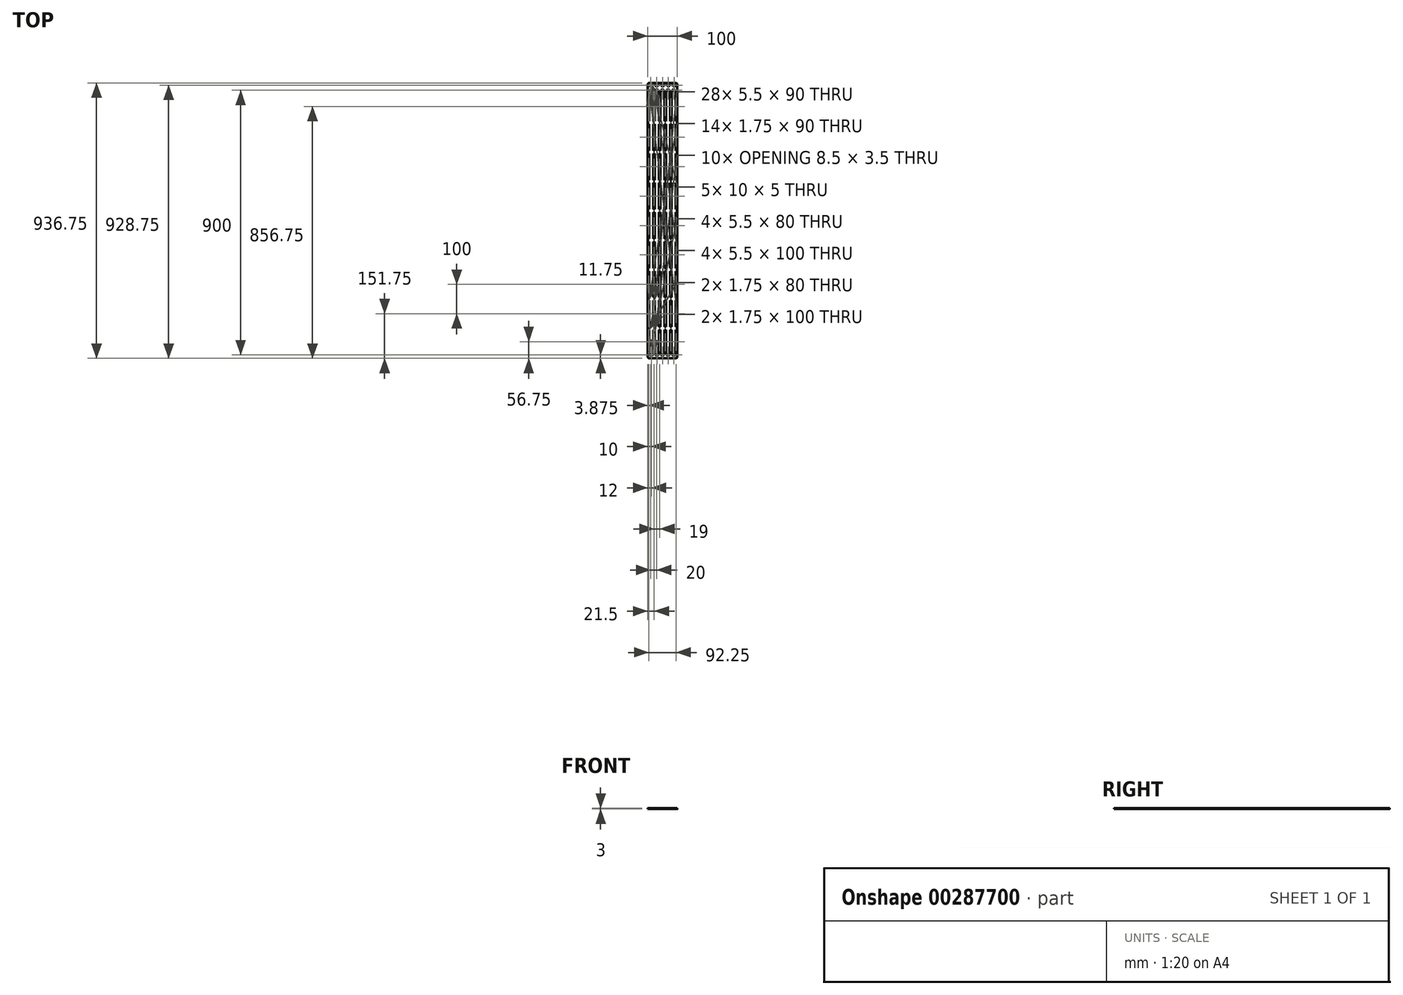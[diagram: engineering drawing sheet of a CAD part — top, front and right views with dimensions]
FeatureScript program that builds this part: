
annotation { "Feature Type Name" : "Feature", "Feature Type Description" : "" }
export const myFeature = defineFeature(function(context is Context, id is Id, definition is map)
    precondition{}
    {
        {
            var Q0;
            Q0=qCreatedBy(makeId("Top.planeOp"),FACE);
            var sketch = newSketch(context, id + "F0", { "sketchPlane" : qUnion([Q0])});
            skLineSegment(sketch, "E0.bottom", {"start": v(-45, 475) * mm, "end": v(45, 475) * mm});
            skLineSegment(sketch, "E0.top", {"start": v(-45, -475) * mm, "end": v(45, -475) * mm});
            skLineSegment(sketch, "E0.left", {"start": v(-50, 470) * mm, "end": v(-50, -456.75) * mm});
            skLineSegment(sketch, "E0.right", {"start": v(50, 470) * mm, "end": v(50, -456.75) * mm});
            skPoint(sketch, "E0.middle", {"position": v(0, 0) * mm});
            skLineSegment(sketch, "E1", {"start": v(-50, 450) * mm, "end": v(50, 450) * mm, "construction": true});
            skLineSegment(sketch, "E2", {"start": v(-50, -450) * mm, "end": v(50, -450) * mm, "construction": true});
            skLineSegment(sketch, "E3.bottom", {"start": v(-3.75, 451.75) * mm, "end": v(3.75, 451.75) * mm});
            skLineSegment(sketch, "E3.top", {"start": v(-3.75, 448.25) * mm, "end": v(3.75, 448.25) * mm});
            skLineSegment(sketch, "E3.left", {"start": v(-4.25, 451.25) * mm, "end": v(-4.25, 448.75) * mm});
            skLineSegment(sketch, "E3.right", {"start": v(4.25, 451.25) * mm, "end": v(4.25, 448.75) * mm});
            skPoint(sketch, "E3.middle", {"position": v(0, 450) * mm});
            skPoint(sketch, "E4.visualSharp", {"position": v(-4.25, 451.75) * mm});
            skArc(sketch, "E4.filletArc", {"start": v(-3.75, 451.75) * mm, "mid": v(-4.1, 451.6) * mm, "end": v(-4.25, 451.25) * mm});
            skPoint(sketch, "E5.visualSharp", {"position": v(-4.25, 448.25) * mm});
            skArc(sketch, "E5.filletArc", {"start": v(-4.25, 448.75) * mm, "mid": v(-4.1, 448.4) * mm, "end": v(-3.75, 448.25) * mm});
            skPoint(sketch, "E6.visualSharp", {"position": v(4.25, 451.75) * mm});
            skArc(sketch, "E6.filletArc", {"start": v(4.25, 451.25) * mm, "mid": v(4.1, 451.6) * mm, "end": v(3.75, 451.75) * mm});
            skPoint(sketch, "E7.visualSharp", {"position": v(4.25, 448.25) * mm});
            skArc(sketch, "E7.filletArc", {"start": v(3.75, 448.25) * mm, "mid": v(4.1, 448.4) * mm, "end": v(4.25, 448.75) * mm});
            skLineSegment(sketch, "E8.1.0.0", {"start": v(15.25, 451.75) * mm, "end": v(22.75, 451.75) * mm});
            skLineSegment(sketch, "E8.1.0.1", {"start": v(23.25, 451.25) * mm, "end": v(23.25, 448.75) * mm});
            skLineSegment(sketch, "E8.1.0.2", {"start": v(14.75, 451.25) * mm, "end": v(14.75, 448.75) * mm});
            skLineSegment(sketch, "E8.1.0.3", {"start": v(15.25, 448.25) * mm, "end": v(22.75, 448.25) * mm});
            skPoint(sketch, "E8.1.0.4", {"position": v(14.75, 448.25) * mm});
            skPoint(sketch, "E8.1.0.5", {"position": v(23.25, 451.75) * mm});
            skPoint(sketch, "E8.1.0.6", {"position": v(19, 450) * mm});
            skPoint(sketch, "E8.1.0.7", {"position": v(23.25, 448.25) * mm});
            skPoint(sketch, "E8.1.0.8", {"position": v(14.75, 451.75) * mm});
            skArc(sketch, "E8.1.0.9", {"start": v(22.75, 448.25) * mm, "mid": v(23.1, 448.4) * mm, "end": v(23.25, 448.75) * mm});
            skArc(sketch, "E8.1.0.10", {"start": v(15.25, 451.75) * mm, "mid": v(14.9, 451.6) * mm, "end": v(14.75, 451.25) * mm});
            skArc(sketch, "E8.1.0.11", {"start": v(14.75, 448.75) * mm, "mid": v(14.9, 448.4) * mm, "end": v(15.25, 448.25) * mm});
            skArc(sketch, "E8.1.0.12", {"start": v(23.25, 451.25) * mm, "mid": v(23.1, 451.6) * mm, "end": v(22.75, 451.75) * mm});
            skLineSegment(sketch, "E8.2.0.0", {"start": v(34.25, 451.75) * mm, "end": v(41.75, 451.75) * mm});
            skLineSegment(sketch, "E8.2.0.1", {"start": v(42.25, 451.25) * mm, "end": v(42.25, 448.75) * mm});
            skLineSegment(sketch, "E8.2.0.2", {"start": v(33.75, 451.25) * mm, "end": v(33.75, 448.75) * mm});
            skLineSegment(sketch, "E8.2.0.3", {"start": v(34.25, 448.25) * mm, "end": v(41.75, 448.25) * mm});
            skPoint(sketch, "E8.2.0.4", {"position": v(33.75, 448.25) * mm});
            skPoint(sketch, "E8.2.0.5", {"position": v(42.25, 451.75) * mm});
            skPoint(sketch, "E8.2.0.6", {"position": v(38, 450) * mm});
            skPoint(sketch, "E8.2.0.7", {"position": v(42.25, 448.25) * mm});
            skPoint(sketch, "E8.2.0.8", {"position": v(33.75, 451.75) * mm});
            skArc(sketch, "E8.2.0.9", {"start": v(41.75, 448.25) * mm, "mid": v(42.1, 448.4) * mm, "end": v(42.25, 448.75) * mm});
            skArc(sketch, "E8.2.0.10", {"start": v(34.25, 451.75) * mm, "mid": v(33.9, 451.6) * mm, "end": v(33.75, 451.25) * mm});
            skArc(sketch, "E8.2.0.11", {"start": v(33.75, 448.75) * mm, "mid": v(33.9, 448.4) * mm, "end": v(34.25, 448.25) * mm});
            skArc(sketch, "E8.2.0.12", {"start": v(42.25, 451.25) * mm, "mid": v(42.1, 451.6) * mm, "end": v(41.75, 451.75) * mm});
            skLineSegment(sketch, "E8.direction1", {"start": v(-4.25, 448.25) * mm, "end": v(14.75, 448.25) * mm, "construction": true});
            skPoint(sketch, "E9.1.0.0", {"position": v(-23.25, 448.25) * mm});
            skPoint(sketch, "E9.1.0.1", {"position": v(-14.75, 448.25) * mm});
            skPoint(sketch, "E9.1.0.2", {"position": v(-19, 450) * mm});
            skPoint(sketch, "E9.1.0.3", {"position": v(-14.75, 451.75) * mm});
            skPoint(sketch, "E9.1.0.4", {"position": v(-23.25, 451.75) * mm});
            skLineSegment(sketch, "E9.1.0.5", {"start": v(-22.75, 451.75) * mm, "end": v(-15.25, 451.75) * mm});
            skLineSegment(sketch, "E9.1.0.6", {"start": v(-22.75, 448.25) * mm, "end": v(-15.25, 448.25) * mm});
            skLineSegment(sketch, "E9.1.0.7", {"start": v(-23.25, 451.25) * mm, "end": v(-23.25, 448.75) * mm});
            skLineSegment(sketch, "E9.1.0.8", {"start": v(-14.75, 451.25) * mm, "end": v(-14.75, 448.75) * mm});
            skArc(sketch, "E9.1.0.9", {"start": v(-14.75, 451.25) * mm, "mid": v(-14.9, 451.6) * mm, "end": v(-15.25, 451.75) * mm});
            skArc(sketch, "E9.1.0.10", {"start": v(-23.25, 448.75) * mm, "mid": v(-23.1, 448.4) * mm, "end": v(-22.75, 448.25) * mm});
            skArc(sketch, "E9.1.0.11", {"start": v(-22.75, 451.75) * mm, "mid": v(-23.1, 451.6) * mm, "end": v(-23.25, 451.25) * mm});
            skArc(sketch, "E9.1.0.12", {"start": v(-15.25, 448.25) * mm, "mid": v(-14.9, 448.4) * mm, "end": v(-14.75, 448.75) * mm});
            skPoint(sketch, "E9.2.0.0", {"position": v(-42.25, 448.25) * mm});
            skPoint(sketch, "E9.2.0.1", {"position": v(-33.75, 448.25) * mm});
            skPoint(sketch, "E9.2.0.2", {"position": v(-38, 450) * mm});
            skPoint(sketch, "E9.2.0.3", {"position": v(-33.75, 451.75) * mm});
            skPoint(sketch, "E9.2.0.4", {"position": v(-42.25, 451.75) * mm});
            skLineSegment(sketch, "E9.2.0.5", {"start": v(-41.75, 451.75) * mm, "end": v(-34.25, 451.75) * mm});
            skLineSegment(sketch, "E9.2.0.6", {"start": v(-41.75, 448.25) * mm, "end": v(-34.25, 448.25) * mm});
            skLineSegment(sketch, "E9.2.0.7", {"start": v(-42.25, 451.25) * mm, "end": v(-42.25, 448.75) * mm});
            skLineSegment(sketch, "E9.2.0.8", {"start": v(-33.75, 451.25) * mm, "end": v(-33.75, 448.75) * mm});
            skArc(sketch, "E9.2.0.9", {"start": v(-33.75, 451.25) * mm, "mid": v(-33.9, 451.6) * mm, "end": v(-34.25, 451.75) * mm});
            skArc(sketch, "E9.2.0.10", {"start": v(-42.25, 448.75) * mm, "mid": v(-42.1, 448.4) * mm, "end": v(-41.75, 448.25) * mm});
            skArc(sketch, "E9.2.0.11", {"start": v(-41.75, 451.75) * mm, "mid": v(-42.1, 451.6) * mm, "end": v(-42.25, 451.25) * mm});
            skArc(sketch, "E9.2.0.12", {"start": v(-34.25, 448.25) * mm, "mid": v(-33.9, 448.4) * mm, "end": v(-33.75, 448.75) * mm});
            skLineSegment(sketch, "E9.direction1", {"start": v(-4.25, 448.25) * mm, "end": v(-23.25, 448.25) * mm, "construction": true});
            skLineSegment(sketch, "E10", {"start": v(-50, 467) * mm, "end": v(50, 467) * mm, "construction": true});
            skLineSegment(sketch, "E11.bottom", {"start": v(-5, 469.5) * mm, "end": v(5, 469.5) * mm});
            skLineSegment(sketch, "E11.top", {"start": v(-5, 464.5) * mm, "end": v(5, 464.5) * mm});
            skLineSegment(sketch, "E11.left", {"start": v(-5, 469.5) * mm, "end": v(-5, 464.5) * mm});
            skLineSegment(sketch, "E11.right", {"start": v(5, 469.5) * mm, "end": v(5, 464.5) * mm});
            skPoint(sketch, "E11.middle", {"position": v(0, 467) * mm});
            skPoint(sketch, "E12.visualSharp", {"position": v(-50, 475) * mm});
            skArc(sketch, "E12.filletArc", {"start": v(-45, 475) * mm, "mid": v(-48.54, 473.54) * mm, "end": v(-50, 470) * mm});
            skPoint(sketch, "E13.visualSharp", {"position": v(50, 475) * mm});
            skArc(sketch, "E13.filletArc", {"start": v(50, 470) * mm, "mid": v(48.54, 473.54) * mm, "end": v(45, 475) * mm});
            skPoint(sketch, "E14.visualSharp", {"position": v(-50, -475) * mm});
            skArc(sketch, "E14.filletArc", {"start": v(-50, -470) * mm, "mid": v(-48.54, -473.54) * mm, "end": v(-45, -475) * mm});
            skPoint(sketch, "E15.visualSharp", {"position": v(50, -475) * mm});
            skArc(sketch, "E15.filletArc", {"start": v(45, -475) * mm, "mid": v(48.54, -473.54) * mm, "end": v(50, -470) * mm});
            skPoint(sketch, "E16.1.0.0", {"position": v(20, 467) * mm});
            skLineSegment(sketch, "E16.1.0.1", {"start": v(25, 469.5) * mm, "end": v(25, 464.5) * mm});
            skLineSegment(sketch, "E16.1.0.2", {"start": v(15, 469.5) * mm, "end": v(25, 469.5) * mm});
            skLineSegment(sketch, "E16.1.0.3", {"start": v(15, 469.5) * mm, "end": v(15, 464.5) * mm});
            skLineSegment(sketch, "E16.1.0.4", {"start": v(15, 464.5) * mm, "end": v(25, 464.5) * mm});
            skPoint(sketch, "E16.2.0.0", {"position": v(40, 467) * mm});
            skLineSegment(sketch, "E16.2.0.1", {"start": v(45, 469.5) * mm, "end": v(45, 464.5) * mm});
            skLineSegment(sketch, "E16.2.0.2", {"start": v(35, 469.5) * mm, "end": v(45, 469.5) * mm});
            skLineSegment(sketch, "E16.2.0.3", {"start": v(35, 469.5) * mm, "end": v(35, 464.5) * mm});
            skLineSegment(sketch, "E16.2.0.4", {"start": v(35, 464.5) * mm, "end": v(45, 464.5) * mm});
            skLineSegment(sketch, "E16.direction1", {"start": v(-5, 464.5) * mm, "end": v(15, 464.5) * mm, "construction": true});
            skLineSegment(sketch, "E17.1.0.0", {"start": v(-15, 469.5) * mm, "end": v(-15, 464.5) * mm});
            skLineSegment(sketch, "E17.1.0.1", {"start": v(-25, 469.5) * mm, "end": v(-25, 464.5) * mm});
            skPoint(sketch, "E17.1.0.2", {"position": v(-20, 467) * mm});
            skLineSegment(sketch, "E17.1.0.3", {"start": v(-25, 464.5) * mm, "end": v(-15, 464.5) * mm});
            skLineSegment(sketch, "E17.1.0.4", {"start": v(-25, 469.5) * mm, "end": v(-15, 469.5) * mm});
            skLineSegment(sketch, "E17.2.0.0", {"start": v(-35, 469.5) * mm, "end": v(-35, 464.5) * mm});
            skLineSegment(sketch, "E17.2.0.1", {"start": v(-45, 469.5) * mm, "end": v(-45, 464.5) * mm});
            skPoint(sketch, "E17.2.0.2", {"position": v(-40, 467) * mm});
            skLineSegment(sketch, "E17.2.0.3", {"start": v(-45, 464.5) * mm, "end": v(-35, 464.5) * mm});
            skLineSegment(sketch, "E17.2.0.4", {"start": v(-45, 469.5) * mm, "end": v(-35, 469.5) * mm});
            skLineSegment(sketch, "E17.direction1", {"start": v(-5, 464.5) * mm, "end": v(-25, 464.5) * mm, "construction": true});
            skArc(sketch, "E18.MirrorCS", {"start": v(-4.25, -448.75) * mm, "mid": v(-4.1, -448.4) * mm, "end": v(-3.75, -448.25) * mm});
            skArc(sketch, "E19.MirrorCS", {"start": v(22.75, -448.25) * mm, "mid": v(23.1, -448.4) * mm, "end": v(23.25, -448.75) * mm});
            skArc(sketch, "E20.MirrorCS", {"start": v(4.25, -451.25) * mm, "mid": v(4.1, -451.6) * mm, "end": v(3.75, -451.75) * mm});
            skArc(sketch, "E21.MirrorCS", {"start": v(-3.75, -451.75) * mm, "mid": v(-4.1, -451.6) * mm, "end": v(-4.25, -451.25) * mm});
            skArc(sketch, "E22.MirrorCS", {"start": v(3.75, -448.25) * mm, "mid": v(4.1, -448.4) * mm, "end": v(4.25, -448.75) * mm});
            skArc(sketch, "E23.MirrorCS", {"start": v(-15.25, -448.25) * mm, "mid": v(-14.9, -448.4) * mm, "end": v(-14.75, -448.75) * mm});
            skArc(sketch, "E24.MirrorCS", {"start": v(-22.75, -451.75) * mm, "mid": v(-23.1, -451.6) * mm, "end": v(-23.25, -451.25) * mm});
            skArc(sketch, "E25.MirrorCS", {"start": v(-34.25, -448.25) * mm, "mid": v(-33.9, -448.4) * mm, "end": v(-33.75, -448.75) * mm});
            skArc(sketch, "E26.MirrorCS", {"start": v(23.25, -451.25) * mm, "mid": v(23.1, -451.6) * mm, "end": v(22.75, -451.75) * mm});
            skArc(sketch, "E27.MirrorCS", {"start": v(33.75, -448.75) * mm, "mid": v(33.9, -448.4) * mm, "end": v(34.25, -448.25) * mm});
            skArc(sketch, "E28.MirrorCS", {"start": v(-42.25, -448.75) * mm, "mid": v(-42.1, -448.4) * mm, "end": v(-41.75, -448.25) * mm});
            skArc(sketch, "E29.MirrorCS", {"start": v(-23.25, -448.75) * mm, "mid": v(-23.1, -448.4) * mm, "end": v(-22.75, -448.25) * mm});
            skArc(sketch, "E30.MirrorCS", {"start": v(42.25, -451.25) * mm, "mid": v(42.1, -451.6) * mm, "end": v(41.75, -451.75) * mm});
            skArc(sketch, "E31.MirrorCS", {"start": v(-41.75, -451.75) * mm, "mid": v(-42.1, -451.6) * mm, "end": v(-42.25, -451.25) * mm});
            skArc(sketch, "E32.MirrorCS", {"start": v(14.75, -448.75) * mm, "mid": v(14.9, -448.4) * mm, "end": v(15.25, -448.25) * mm});
            skArc(sketch, "E33.MirrorCS", {"start": v(34.25, -451.75) * mm, "mid": v(33.9, -451.6) * mm, "end": v(33.75, -451.25) * mm});
            skArc(sketch, "E34.MirrorCS", {"start": v(-33.75, -451.25) * mm, "mid": v(-33.9, -451.6) * mm, "end": v(-34.25, -451.75) * mm});
            skArc(sketch, "E35.MirrorCS", {"start": v(-14.75, -451.25) * mm, "mid": v(-14.9, -451.6) * mm, "end": v(-15.25, -451.75) * mm});
            skArc(sketch, "E36.MirrorCS", {"start": v(15.25, -451.75) * mm, "mid": v(14.9, -451.6) * mm, "end": v(14.75, -451.25) * mm});
            skArc(sketch, "E37.MirrorCS", {"start": v(41.75, -448.25) * mm, "mid": v(42.1, -448.4) * mm, "end": v(42.25, -448.75) * mm});
            skLineSegment(sketch, "E38.MirrorCS", {"start": v(-14.75, -451.25) * mm, "end": v(-14.75, -448.75) * mm});
            skLineSegment(sketch, "E39.MirrorCS", {"start": v(-22.75, -448.25) * mm, "end": v(-15.25, -448.25) * mm});
            skLineSegment(sketch, "E40.MirrorCS", {"start": v(-3.75, -448.25) * mm, "end": v(3.75, -448.25) * mm});
            skPoint(sketch, "E41.MirrorP", {"position": v(33.75, -448.25) * mm});
            skLineSegment(sketch, "E42.MirrorCS", {"start": v(34.25, -448.25) * mm, "end": v(41.75, -448.25) * mm});
            skLineSegment(sketch, "E43.MirrorCS", {"start": v(-42.25, -451.25) * mm, "end": v(-42.25, -448.75) * mm});
            skPoint(sketch, "E44.MirrorP", {"position": v(19, -450) * mm});
            skPoint(sketch, "E45.MirrorP", {"position": v(-23.25, -448.25) * mm});
            skPoint(sketch, "E46.MirrorP", {"position": v(-4.25, -451.75) * mm});
            skLineSegment(sketch, "E47.MirrorCS", {"start": v(-23.25, -451.25) * mm, "end": v(-23.25, -448.75) * mm});
            skLineSegment(sketch, "E48.MirrorCS", {"start": v(15.25, -448.25) * mm, "end": v(22.75, -448.25) * mm});
            skPoint(sketch, "E49.MirrorP", {"position": v(23.25, -451.75) * mm});
            skLineSegment(sketch, "E50.MirrorCS", {"start": v(33.75, -451.25) * mm, "end": v(33.75, -448.75) * mm});
            skLineSegment(sketch, "E51.MirrorCS", {"start": v(-41.75, -448.25) * mm, "end": v(-34.25, -448.25) * mm});
            skLineSegment(sketch, "E52.MirrorCS", {"start": v(14.75, -451.25) * mm, "end": v(14.75, -448.75) * mm});
            skPoint(sketch, "E53.MirrorP", {"position": v(14.75, -448.25) * mm});
            skLineSegment(sketch, "E54.MirrorCS", {"start": v(42.25, -451.25) * mm, "end": v(42.25, -448.75) * mm});
            skLineSegment(sketch, "E55.MirrorCS", {"start": v(-41.75, -451.75) * mm, "end": v(-34.25, -451.75) * mm});
            skPoint(sketch, "E56.MirrorP", {"position": v(0, -450) * mm});
            skLineSegment(sketch, "E57.MirrorCS", {"start": v(4.25, -451.25) * mm, "end": v(4.25, -448.75) * mm});
            skLineSegment(sketch, "E58.MirrorCS", {"start": v(-4.25, -451.25) * mm, "end": v(-4.25, -448.75) * mm});
            skLineSegment(sketch, "E59.MirrorCS", {"start": v(-3.75, -451.75) * mm, "end": v(3.75, -451.75) * mm});
            skLineSegment(sketch, "E60.MirrorCS", {"start": v(23.25, -451.25) * mm, "end": v(23.25, -448.75) * mm});
            skLineSegment(sketch, "E61.MirrorCS", {"start": v(15.25, -451.75) * mm, "end": v(22.75, -451.75) * mm});
            skLineSegment(sketch, "E62.MirrorCS", {"start": v(-22.75, -451.75) * mm, "end": v(-15.25, -451.75) * mm});
            skLineSegment(sketch, "E63.MirrorCS", {"start": v(-4.25, -448.25) * mm, "end": v(-23.25, -448.25) * mm, "construction": true});
            skLineSegment(sketch, "E64.MirrorCS", {"start": v(34.25, -451.75) * mm, "end": v(41.75, -451.75) * mm});
            skPoint(sketch, "E65.MirrorP", {"position": v(-23.25, -451.75) * mm});
            skPoint(sketch, "E66.MirrorP", {"position": v(-42.25, -451.75) * mm});
            skPoint(sketch, "E67.MirrorP", {"position": v(-33.75, -448.25) * mm});
            skPoint(sketch, "E68.MirrorP", {"position": v(4.25, -451.75) * mm});
            skPoint(sketch, "E69.MirrorP", {"position": v(42.25, -448.25) * mm});
            skLineSegment(sketch, "E70.MirrorCS", {"start": v(-4.25, -448.25) * mm, "end": v(14.75, -448.25) * mm, "construction": true});
            skPoint(sketch, "E71.MirrorP", {"position": v(4.25, -448.25) * mm});
            skPoint(sketch, "E72.MirrorP", {"position": v(-14.75, -451.75) * mm});
            skPoint(sketch, "E73.MirrorP", {"position": v(-33.75, -451.75) * mm});
            skPoint(sketch, "E74.MirrorP", {"position": v(-42.25, -448.25) * mm});
            skPoint(sketch, "E75.MirrorP", {"position": v(38, -450) * mm});
            skPoint(sketch, "E76.MirrorP", {"position": v(14.75, -451.75) * mm});
            skPoint(sketch, "E77.MirrorP", {"position": v(33.75, -451.75) * mm});
            skPoint(sketch, "E78.MirrorP", {"position": v(-19, -450) * mm});
            skPoint(sketch, "E79.MirrorP", {"position": v(-38, -450) * mm});
            skPoint(sketch, "E80.MirrorP", {"position": v(-4.25, -448.25) * mm});
            skPoint(sketch, "E81.MirrorP", {"position": v(42.25, -451.75) * mm});
            skLineSegment(sketch, "E82.MirrorCS", {"start": v(-33.75, -451.25) * mm, "end": v(-33.75, -448.75) * mm});
            skPoint(sketch, "E83.MirrorP", {"position": v(23.25, -448.25) * mm});
            skPoint(sketch, "E84.MirrorP", {"position": v(-14.75, -448.25) * mm});
            skLineSegment(sketch, "E85", {"start": v(-45, -461.75) * mm, "end": v(45, -461.75) * mm});
            skArc(sketch, "E86.filletArc", {"start": v(-50, -456.75) * mm, "mid": v(-48.54, -460.29) * mm, "end": v(-45, -461.75) * mm});
            skArc(sketch, "E87.filletArc", {"start": v(45, -461.75) * mm, "mid": v(48.54, -460.29) * mm, "end": v(50, -456.75) * mm});
            skLineSegment(sketch, "E88.bottom", {"start": v(-31.25, 445) * mm, "end": v(-25.75, 445) * mm});
            skLineSegment(sketch, "E88.top", {"start": v(-31.25, -445) * mm, "end": v(-25.75, -445) * mm});
            skLineSegment(sketch, "E88.left", {"start": v(-31.25, 445) * mm, "end": v(-31.25, -445) * mm});
            skLineSegment(sketch, "E88.right", {"start": v(-25.75, 445) * mm, "end": v(-25.75, -445) * mm});
            skLineSegment(sketch, "E89.1.0.0", {"start": v(-12.25, 445) * mm, "end": v(-12.25, -445) * mm});
            skLineSegment(sketch, "E89.1.0.1", {"start": v(-12.25, 445) * mm, "end": v(-6.75, 445) * mm});
            skLineSegment(sketch, "E89.1.0.2", {"start": v(-6.75, 445) * mm, "end": v(-6.75, -445) * mm});
            skLineSegment(sketch, "E89.1.0.3", {"start": v(-12.25, -445) * mm, "end": v(-6.75, -445) * mm});
            skLineSegment(sketch, "E89.2.0.0", {"start": v(6.75, 445) * mm, "end": v(6.75, -445) * mm});
            skLineSegment(sketch, "E89.2.0.1", {"start": v(6.75, 445) * mm, "end": v(12.25, 445) * mm});
            skLineSegment(sketch, "E89.2.0.2", {"start": v(12.25, 445) * mm, "end": v(12.25, -445) * mm});
            skLineSegment(sketch, "E89.2.0.3", {"start": v(6.75, -445) * mm, "end": v(12.25, -445) * mm});
            skLineSegment(sketch, "E89.3.0.0", {"start": v(25.75, 445) * mm, "end": v(25.75, -445) * mm});
            skLineSegment(sketch, "E89.3.0.1", {"start": v(25.75, 445) * mm, "end": v(31.25, 445) * mm});
            skLineSegment(sketch, "E89.3.0.2", {"start": v(31.25, 445) * mm, "end": v(31.25, -445) * mm});
            skLineSegment(sketch, "E89.3.0.3", {"start": v(25.75, -445) * mm, "end": v(31.25, -445) * mm});
            skLineSegment(sketch, "E89.direction1", {"start": v(-31.25, -445) * mm, "end": v(-12.25, -445) * mm, "construction": true});
            skLineSegment(sketch, "E90", {"start": v(-47, 445) * mm, "end": v(-45.25, 445) * mm});
            skLineSegment(sketch, "E91", {"start": v(-45.25, 445) * mm, "end": v(-45.25, -445) * mm});
            skLineSegment(sketch, "E92", {"start": v(-45.25, -445) * mm, "end": v(-47, -445) * mm});
            skLineSegment(sketch, "E93", {"start": v(-47, -445) * mm, "end": v(-47, 445) * mm});
            skLineSegment(sketch, "E94.MirrorCS", {"start": v(47, 445) * mm, "end": v(45.25, 445) * mm});
            skLineSegment(sketch, "E95.MirrorCS", {"start": v(47, -445) * mm, "end": v(47, 445) * mm});
            skLineSegment(sketch, "E96.MirrorCS", {"start": v(45.25, 445) * mm, "end": v(45.25, -445) * mm});
            skLineSegment(sketch, "E97.MirrorCS", {"start": v(45.25, -445) * mm, "end": v(47, -445) * mm});
            skLineSegment(sketch, "E98", {"start": v(-47, 345) * mm, "end": v(-45.25, 345) * mm});
            skLineSegment(sketch, "E99", {"start": v(-31.25, 345) * mm, "end": v(-25.75, 345) * mm});
            skLineSegment(sketch, "E100", {"start": v(-12.25, 345) * mm, "end": v(-6.75, 345) * mm});
            skLineSegment(sketch, "E101", {"start": v(6.75, 345) * mm, "end": v(12.25, 345) * mm});
            skLineSegment(sketch, "E102", {"start": v(25.75, 345) * mm, "end": v(31.25, 345) * mm});
            skLineSegment(sketch, "E103", {"start": v(45.25, 345) * mm, "end": v(47, 345) * mm});
            skLineSegment(sketch, "E104", {"start": v(-47, 335) * mm, "end": v(-45.25, 335) * mm});
            skLineSegment(sketch, "E105", {"start": v(-31.25, 335) * mm, "end": v(-25.75, 335) * mm});
            skLineSegment(sketch, "E106", {"start": v(-12.25, 335) * mm, "end": v(-6.75, 335) * mm});
            skLineSegment(sketch, "E107", {"start": v(6.75, 335) * mm, "end": v(12.25, 335) * mm});
            skLineSegment(sketch, "E108", {"start": v(25.75, 335) * mm, "end": v(31.25, 335) * mm});
            skLineSegment(sketch, "E109", {"start": v(45.25, 335) * mm, "end": v(47, 335) * mm});
            skLineSegment(sketch, "E110.0.1.0", {"start": v(-47, 245) * mm, "end": v(-45.25, 245) * mm});
            skLineSegment(sketch, "E110.0.1.1", {"start": v(-47, 235) * mm, "end": v(-45.25, 235) * mm});
            skLineSegment(sketch, "E110.0.1.2", {"start": v(-31.25, 245) * mm, "end": v(-25.75, 245) * mm});
            skLineSegment(sketch, "E110.0.1.3", {"start": v(-31.25, 235) * mm, "end": v(-25.75, 235) * mm});
            skLineSegment(sketch, "E110.0.1.4", {"start": v(-12.25, 245) * mm, "end": v(-6.75, 245) * mm});
            skLineSegment(sketch, "E110.0.1.5", {"start": v(-12.25, 235) * mm, "end": v(-6.75, 235) * mm});
            skLineSegment(sketch, "E110.0.1.6", {"start": v(6.75, 245) * mm, "end": v(12.25, 245) * mm});
            skLineSegment(sketch, "E110.0.1.7", {"start": v(6.75, 235) * mm, "end": v(12.25, 235) * mm});
            skLineSegment(sketch, "E110.0.1.8", {"start": v(25.75, 245) * mm, "end": v(31.25, 245) * mm});
            skLineSegment(sketch, "E110.0.1.9", {"start": v(25.75, 235) * mm, "end": v(31.25, 235) * mm});
            skLineSegment(sketch, "E110.0.1.10", {"start": v(45.25, 245) * mm, "end": v(47, 245) * mm});
            skLineSegment(sketch, "E110.0.1.11", {"start": v(45.25, 235) * mm, "end": v(47, 235) * mm});
            skLineSegment(sketch, "E110.0.2.0", {"start": v(-47, 145) * mm, "end": v(-45.25, 145) * mm});
            skLineSegment(sketch, "E110.0.2.1", {"start": v(-47, 135) * mm, "end": v(-45.25, 135) * mm});
            skLineSegment(sketch, "E110.0.2.2", {"start": v(-31.25, 145) * mm, "end": v(-25.75, 145) * mm});
            skLineSegment(sketch, "E110.0.2.3", {"start": v(-31.25, 135) * mm, "end": v(-25.75, 135) * mm});
            skLineSegment(sketch, "E110.0.2.4", {"start": v(-12.25, 145) * mm, "end": v(-6.75, 145) * mm});
            skLineSegment(sketch, "E110.0.2.5", {"start": v(-12.25, 135) * mm, "end": v(-6.75, 135) * mm});
            skLineSegment(sketch, "E110.0.2.6", {"start": v(6.75, 145) * mm, "end": v(12.25, 145) * mm});
            skLineSegment(sketch, "E110.0.2.7", {"start": v(6.75, 135) * mm, "end": v(12.25, 135) * mm});
            skLineSegment(sketch, "E110.0.2.8", {"start": v(25.75, 145) * mm, "end": v(31.25, 145) * mm});
            skLineSegment(sketch, "E110.0.2.9", {"start": v(25.75, 135) * mm, "end": v(31.25, 135) * mm});
            skLineSegment(sketch, "E110.0.2.10", {"start": v(45.25, 145) * mm, "end": v(47, 145) * mm});
            skLineSegment(sketch, "E110.0.2.11", {"start": v(45.25, 135) * mm, "end": v(47, 135) * mm});
            skLineSegment(sketch, "E110.0.3.0", {"start": v(-47, 45) * mm, "end": v(-45.25, 45) * mm});
            skLineSegment(sketch, "E110.0.3.1", {"start": v(-47, 35) * mm, "end": v(-45.25, 35) * mm});
            skLineSegment(sketch, "E110.0.3.2", {"start": v(-31.25, 45) * mm, "end": v(-25.75, 45) * mm});
            skLineSegment(sketch, "E110.0.3.3", {"start": v(-31.25, 35) * mm, "end": v(-25.75, 35) * mm});
            skLineSegment(sketch, "E110.0.3.4", {"start": v(-12.25, 45) * mm, "end": v(-6.75, 45) * mm});
            skLineSegment(sketch, "E110.0.3.5", {"start": v(-12.25, 35) * mm, "end": v(-6.75, 35) * mm});
            skLineSegment(sketch, "E110.0.3.6", {"start": v(6.75, 45) * mm, "end": v(12.25, 45) * mm});
            skLineSegment(sketch, "E110.0.3.7", {"start": v(6.75, 35) * mm, "end": v(12.25, 35) * mm});
            skLineSegment(sketch, "E110.0.3.8", {"start": v(25.75, 45) * mm, "end": v(31.25, 45) * mm});
            skLineSegment(sketch, "E110.0.3.9", {"start": v(25.75, 35) * mm, "end": v(31.25, 35) * mm});
            skLineSegment(sketch, "E110.0.3.10", {"start": v(45.25, 45) * mm, "end": v(47, 45) * mm});
            skLineSegment(sketch, "E110.0.3.11", {"start": v(45.25, 35) * mm, "end": v(47, 35) * mm});
            skLineSegment(sketch, "E110.0.4.0", {"start": v(-47, -55) * mm, "end": v(-45.25, -55) * mm});
            skLineSegment(sketch, "E110.0.4.1", {"start": v(-47, -65) * mm, "end": v(-45.25, -65) * mm});
            skLineSegment(sketch, "E110.0.4.2", {"start": v(-31.25, -55) * mm, "end": v(-25.75, -55) * mm});
            skLineSegment(sketch, "E110.0.4.3", {"start": v(-31.25, -65) * mm, "end": v(-25.75, -65) * mm});
            skLineSegment(sketch, "E110.0.4.4", {"start": v(-12.25, -55) * mm, "end": v(-6.75, -55) * mm});
            skLineSegment(sketch, "E110.0.4.5", {"start": v(-12.25, -65) * mm, "end": v(-6.75, -65) * mm});
            skLineSegment(sketch, "E110.0.4.6", {"start": v(6.75, -55) * mm, "end": v(12.25, -55) * mm});
            skLineSegment(sketch, "E110.0.4.7", {"start": v(6.75, -65) * mm, "end": v(12.25, -65) * mm});
            skLineSegment(sketch, "E110.0.4.8", {"start": v(25.75, -55) * mm, "end": v(31.25, -55) * mm});
            skLineSegment(sketch, "E110.0.4.9", {"start": v(25.75, -65) * mm, "end": v(31.25, -65) * mm});
            skLineSegment(sketch, "E110.0.4.10", {"start": v(45.25, -55) * mm, "end": v(47, -55) * mm});
            skLineSegment(sketch, "E110.0.4.11", {"start": v(45.25, -65) * mm, "end": v(47, -65) * mm});
            skLineSegment(sketch, "E110.0.5.0", {"start": v(-47, -155) * mm, "end": v(-45.25, -155) * mm});
            skLineSegment(sketch, "E110.0.5.1", {"start": v(-47, -165) * mm, "end": v(-45.25, -165) * mm});
            skLineSegment(sketch, "E110.0.5.2", {"start": v(-31.25, -155) * mm, "end": v(-25.75, -155) * mm});
            skLineSegment(sketch, "E110.0.5.3", {"start": v(-31.25, -165) * mm, "end": v(-25.75, -165) * mm});
            skLineSegment(sketch, "E110.0.5.4", {"start": v(-12.25, -155) * mm, "end": v(-6.75, -155) * mm});
            skLineSegment(sketch, "E110.0.5.5", {"start": v(-12.25, -165) * mm, "end": v(-6.75, -165) * mm});
            skLineSegment(sketch, "E110.0.5.6", {"start": v(6.75, -155) * mm, "end": v(12.25, -155) * mm});
            skLineSegment(sketch, "E110.0.5.7", {"start": v(6.75, -165) * mm, "end": v(12.25, -165) * mm});
            skLineSegment(sketch, "E110.0.5.8", {"start": v(25.75, -155) * mm, "end": v(31.25, -155) * mm});
            skLineSegment(sketch, "E110.0.5.9", {"start": v(25.75, -165) * mm, "end": v(31.25, -165) * mm});
            skLineSegment(sketch, "E110.0.5.10", {"start": v(45.25, -155) * mm, "end": v(47, -155) * mm});
            skLineSegment(sketch, "E110.0.5.11", {"start": v(45.25, -165) * mm, "end": v(47, -165) * mm});
            skLineSegment(sketch, "E110.0.6.0", {"start": v(-47, -255) * mm, "end": v(-45.25, -255) * mm});
            skLineSegment(sketch, "E110.0.6.1", {"start": v(-47, -265) * mm, "end": v(-45.25, -265) * mm});
            skLineSegment(sketch, "E110.0.6.2", {"start": v(-31.25, -255) * mm, "end": v(-25.75, -255) * mm});
            skLineSegment(sketch, "E110.0.6.3", {"start": v(-31.25, -265) * mm, "end": v(-25.75, -265) * mm});
            skLineSegment(sketch, "E110.0.6.4", {"start": v(-12.25, -255) * mm, "end": v(-6.75, -255) * mm});
            skLineSegment(sketch, "E110.0.6.5", {"start": v(-12.25, -265) * mm, "end": v(-6.75, -265) * mm});
            skLineSegment(sketch, "E110.0.6.6", {"start": v(6.75, -255) * mm, "end": v(12.25, -255) * mm});
            skLineSegment(sketch, "E110.0.6.7", {"start": v(6.75, -265) * mm, "end": v(12.25, -265) * mm});
            skLineSegment(sketch, "E110.0.6.8", {"start": v(25.75, -255) * mm, "end": v(31.25, -255) * mm});
            skLineSegment(sketch, "E110.0.6.9", {"start": v(25.75, -265) * mm, "end": v(31.25, -265) * mm});
            skLineSegment(sketch, "E110.0.6.10", {"start": v(45.25, -255) * mm, "end": v(47, -255) * mm});
            skLineSegment(sketch, "E110.0.6.11", {"start": v(45.25, -265) * mm, "end": v(47, -265) * mm});
            skLineSegment(sketch, "E110.0.7.0", {"start": v(-47, -355) * mm, "end": v(-45.25, -355) * mm});
            skLineSegment(sketch, "E110.0.7.1", {"start": v(-47, -365) * mm, "end": v(-45.25, -365) * mm});
            skLineSegment(sketch, "E110.0.7.2", {"start": v(-31.25, -355) * mm, "end": v(-25.75, -355) * mm});
            skLineSegment(sketch, "E110.0.7.3", {"start": v(-31.25, -365) * mm, "end": v(-25.75, -365) * mm});
            skLineSegment(sketch, "E110.0.7.4", {"start": v(-12.25, -355) * mm, "end": v(-6.75, -355) * mm});
            skLineSegment(sketch, "E110.0.7.5", {"start": v(-12.25, -365) * mm, "end": v(-6.75, -365) * mm});
            skLineSegment(sketch, "E110.0.7.6", {"start": v(6.75, -355) * mm, "end": v(12.25, -355) * mm});
            skLineSegment(sketch, "E110.0.7.7", {"start": v(6.75, -365) * mm, "end": v(12.25, -365) * mm});
            skLineSegment(sketch, "E110.0.7.8", {"start": v(25.75, -355) * mm, "end": v(31.25, -355) * mm});
            skLineSegment(sketch, "E110.0.7.9", {"start": v(25.75, -365) * mm, "end": v(31.25, -365) * mm});
            skLineSegment(sketch, "E110.0.7.10", {"start": v(45.25, -355) * mm, "end": v(47, -355) * mm});
            skLineSegment(sketch, "E110.0.7.11", {"start": v(45.25, -365) * mm, "end": v(47, -365) * mm});
            skLineSegment(sketch, "E110.direction1", {"start": v(-47, 335) * mm, "end": v(-22, 335) * mm, "construction": true});
            skLineSegment(sketch, "E110.direction2", {"start": v(-47, 335) * mm, "end": v(-47, 235) * mm, "construction": true});
            skSolve(sketch);
        }
        {
            var Q0;
            {var subQ0=sQuery(id+"F0.wireOp",EDGE,"E110.0.5.0");Q0=makeQuery(id+"F0.imprint","IMPRINT",FACE,{"disambiguationData":[TD([[makeQuery(id+"F0.imprint","IMPRINT",EDGE,{"derivedFrom":subQ0}),-1.0]])]});}
            var Q1;
            {var subQ0=sQuery(id+"F0.wireOp",EDGE,"E110.0.5.2");Q1=makeQuery(id+"F0.imprint","IMPRINT",FACE,{"disambiguationData":[TD([[makeQuery(id+"F0.imprint","IMPRINT",EDGE,{"derivedFrom":subQ0}),-1.0]])]});}
            var Q2;
            {var subQ0=sQuery(id+"F0.wireOp",EDGE,"E110.0.5.4");Q2=makeQuery(id+"F0.imprint","IMPRINT",FACE,{"disambiguationData":[TD([[makeQuery(id+"F0.imprint","IMPRINT",EDGE,{"derivedFrom":subQ0}),-1.0]])]});}
            var Q3;
            {var subQ0=sQuery(id+"F0.wireOp",EDGE,"E110.0.5.6");Q3=makeQuery(id+"F0.imprint","IMPRINT",FACE,{"disambiguationData":[TD([[makeQuery(id+"F0.imprint","IMPRINT",EDGE,{"derivedFrom":subQ0}),-1.0]])]});}
            var Q4;
            {var subQ0=sQuery(id+"F0.wireOp",EDGE,"E110.0.5.8");Q4=makeQuery(id+"F0.imprint","IMPRINT",FACE,{"disambiguationData":[TD([[makeQuery(id+"F0.imprint","IMPRINT",EDGE,{"derivedFrom":subQ0}),-1.0]])]});}
            var Q5;
            {var subQ0=sQuery(id+"F0.wireOp",EDGE,"E110.0.5.10");Q5=makeQuery(id+"F0.imprint","IMPRINT",FACE,{"disambiguationData":[TD([[makeQuery(id+"F0.imprint","IMPRINT",EDGE,{"derivedFrom":subQ0}),-1.0]])]});}
            var Q6;
            Q6=makeQuery(id+"F0.imprint","IMPRINT",FACE,{"disambiguationData":[TD([[makeQuery(id+"F0.imprint","IMPRINT",EDGE,{"derivedFrom":sQuery(id+"F0.wireOp",EDGE,"E0.bottom")}),-1.0]])]});
            var Q7;
            {var subQ0=sQuery(id+"F0.wireOp",EDGE,"E110.0.6.0");Q7=makeQuery(id+"F0.imprint","IMPRINT",FACE,{"disambiguationData":[TD([[makeQuery(id+"F0.imprint","IMPRINT",EDGE,{"derivedFrom":subQ0}),-1.0]])]});}
            var Q8;
            {var subQ0=sQuery(id+"F0.wireOp",EDGE,"E110.0.6.2");Q8=makeQuery(id+"F0.imprint","IMPRINT",FACE,{"disambiguationData":[TD([[makeQuery(id+"F0.imprint","IMPRINT",EDGE,{"derivedFrom":subQ0}),-1.0]])]});}
            var Q9;
            {var subQ0=sQuery(id+"F0.wireOp",EDGE,"E110.0.6.4");Q9=makeQuery(id+"F0.imprint","IMPRINT",FACE,{"disambiguationData":[TD([[makeQuery(id+"F0.imprint","IMPRINT",EDGE,{"derivedFrom":subQ0}),-1.0]])]});}
            var Q10;
            {var subQ0=sQuery(id+"F0.wireOp",EDGE,"E110.0.6.6");Q10=makeQuery(id+"F0.imprint","IMPRINT",FACE,{"disambiguationData":[TD([[makeQuery(id+"F0.imprint","IMPRINT",EDGE,{"derivedFrom":subQ0}),-1.0]])]});}
            var Q11;
            {var subQ0=sQuery(id+"F0.wireOp",EDGE,"E110.0.6.8");Q11=makeQuery(id+"F0.imprint","IMPRINT",FACE,{"disambiguationData":[TD([[makeQuery(id+"F0.imprint","IMPRINT",EDGE,{"derivedFrom":subQ0}),-1.0]])]});}
            var Q12;
            {var subQ0=sQuery(id+"F0.wireOp",EDGE,"E110.0.6.10");Q12=makeQuery(id+"F0.imprint","IMPRINT",FACE,{"disambiguationData":[TD([[makeQuery(id+"F0.imprint","IMPRINT",EDGE,{"derivedFrom":subQ0}),-1.0]])]});}
            var Q13;
            {var subQ0=sQuery(id+"F0.wireOp",EDGE,"E110.0.7.0");Q13=makeQuery(id+"F0.imprint","IMPRINT",FACE,{"disambiguationData":[TD([[makeQuery(id+"F0.imprint","IMPRINT",EDGE,{"derivedFrom":subQ0}),-1.0]])]});}
            var Q14;
            {var subQ0=sQuery(id+"F0.wireOp",EDGE,"E110.0.7.2");Q14=makeQuery(id+"F0.imprint","IMPRINT",FACE,{"disambiguationData":[TD([[makeQuery(id+"F0.imprint","IMPRINT",EDGE,{"derivedFrom":subQ0}),-1.0]])]});}
            var Q15;
            {var subQ0=sQuery(id+"F0.wireOp",EDGE,"E110.0.7.4");Q15=makeQuery(id+"F0.imprint","IMPRINT",FACE,{"disambiguationData":[TD([[makeQuery(id+"F0.imprint","IMPRINT",EDGE,{"derivedFrom":subQ0}),-1.0]])]});}
            var Q16;
            {var subQ0=sQuery(id+"F0.wireOp",EDGE,"E110.0.7.8");Q16=makeQuery(id+"F0.imprint","IMPRINT",FACE,{"disambiguationData":[TD([[makeQuery(id+"F0.imprint","IMPRINT",EDGE,{"derivedFrom":subQ0}),-1.0]])]});}
            var Q17;
            {var subQ0=sQuery(id+"F0.wireOp",EDGE,"E110.0.7.10");Q17=makeQuery(id+"F0.imprint","IMPRINT",FACE,{"disambiguationData":[TD([[makeQuery(id+"F0.imprint","IMPRINT",EDGE,{"derivedFrom":subQ0}),-1.0]])]});}
            var Q18;
            {var subQ0=sQuery(id+"F0.wireOp",EDGE,"E110.0.7.6");Q18=makeQuery(id+"F0.imprint","IMPRINT",FACE,{"disambiguationData":[TD([[makeQuery(id+"F0.imprint","IMPRINT",EDGE,{"derivedFrom":subQ0}),-1.0]])]});}
            var Q19;
            {var subQ0=sQuery(id+"F0.wireOp",EDGE,"E110.0.4.0");Q19=makeQuery(id+"F0.imprint","IMPRINT",FACE,{"disambiguationData":[TD([[makeQuery(id+"F0.imprint","IMPRINT",EDGE,{"derivedFrom":subQ0}),-1.0]])]});}
            var Q20;
            {var subQ0=sQuery(id+"F0.wireOp",EDGE,"E110.0.4.2");Q20=makeQuery(id+"F0.imprint","IMPRINT",FACE,{"disambiguationData":[TD([[makeQuery(id+"F0.imprint","IMPRINT",EDGE,{"derivedFrom":subQ0}),-1.0]])]});}
            var Q21;
            {var subQ0=sQuery(id+"F0.wireOp",EDGE,"E110.0.4.4");Q21=makeQuery(id+"F0.imprint","IMPRINT",FACE,{"disambiguationData":[TD([[makeQuery(id+"F0.imprint","IMPRINT",EDGE,{"derivedFrom":subQ0}),-1.0]])]});}
            var Q22;
            {var subQ0=sQuery(id+"F0.wireOp",EDGE,"E110.0.4.6");Q22=makeQuery(id+"F0.imprint","IMPRINT",FACE,{"disambiguationData":[TD([[makeQuery(id+"F0.imprint","IMPRINT",EDGE,{"derivedFrom":subQ0}),-1.0]])]});}
            var Q23;
            {var subQ0=sQuery(id+"F0.wireOp",EDGE,"E110.0.4.8");Q23=makeQuery(id+"F0.imprint","IMPRINT",FACE,{"disambiguationData":[TD([[makeQuery(id+"F0.imprint","IMPRINT",EDGE,{"derivedFrom":subQ0}),-1.0]])]});}
            var Q24;
            {var subQ0=sQuery(id+"F0.wireOp",EDGE,"E110.0.4.10");Q24=makeQuery(id+"F0.imprint","IMPRINT",FACE,{"disambiguationData":[TD([[makeQuery(id+"F0.imprint","IMPRINT",EDGE,{"derivedFrom":subQ0}),-1.0]])]});}
            var Q25;
            {var subQ0=sQuery(id+"F0.wireOp",EDGE,"E110.0.3.0");Q25=makeQuery(id+"F0.imprint","IMPRINT",FACE,{"disambiguationData":[TD([[makeQuery(id+"F0.imprint","IMPRINT",EDGE,{"derivedFrom":subQ0}),-1.0]])]});}
            var Q26;
            {var subQ0=sQuery(id+"F0.wireOp",EDGE,"E110.0.3.2");Q26=makeQuery(id+"F0.imprint","IMPRINT",FACE,{"disambiguationData":[TD([[makeQuery(id+"F0.imprint","IMPRINT",EDGE,{"derivedFrom":subQ0}),-1.0]])]});}
            var Q27;
            {var subQ0=sQuery(id+"F0.wireOp",EDGE,"E110.0.3.4");Q27=makeQuery(id+"F0.imprint","IMPRINT",FACE,{"disambiguationData":[TD([[makeQuery(id+"F0.imprint","IMPRINT",EDGE,{"derivedFrom":subQ0}),-1.0]])]});}
            var Q28;
            {var subQ0=sQuery(id+"F0.wireOp",EDGE,"E110.0.3.6");Q28=makeQuery(id+"F0.imprint","IMPRINT",FACE,{"disambiguationData":[TD([[makeQuery(id+"F0.imprint","IMPRINT",EDGE,{"derivedFrom":subQ0}),-1.0]])]});}
            var Q29;
            {var subQ0=sQuery(id+"F0.wireOp",EDGE,"E110.0.3.8");Q29=makeQuery(id+"F0.imprint","IMPRINT",FACE,{"disambiguationData":[TD([[makeQuery(id+"F0.imprint","IMPRINT",EDGE,{"derivedFrom":subQ0}),-1.0]])]});}
            var Q30;
            {var subQ0=sQuery(id+"F0.wireOp",EDGE,"E110.0.3.10");Q30=makeQuery(id+"F0.imprint","IMPRINT",FACE,{"disambiguationData":[TD([[makeQuery(id+"F0.imprint","IMPRINT",EDGE,{"derivedFrom":subQ0}),-1.0]])]});}
            var Q31;
            {var subQ0=sQuery(id+"F0.wireOp",EDGE,"E110.0.2.0");Q31=makeQuery(id+"F0.imprint","IMPRINT",FACE,{"disambiguationData":[TD([[makeQuery(id+"F0.imprint","IMPRINT",EDGE,{"derivedFrom":subQ0}),-1.0]])]});}
            var Q32;
            {var subQ0=sQuery(id+"F0.wireOp",EDGE,"E110.0.2.2");Q32=makeQuery(id+"F0.imprint","IMPRINT",FACE,{"disambiguationData":[TD([[makeQuery(id+"F0.imprint","IMPRINT",EDGE,{"derivedFrom":subQ0}),-1.0]])]});}
            var Q33;
            {var subQ0=sQuery(id+"F0.wireOp",EDGE,"E110.0.2.4");Q33=makeQuery(id+"F0.imprint","IMPRINT",FACE,{"disambiguationData":[TD([[makeQuery(id+"F0.imprint","IMPRINT",EDGE,{"derivedFrom":subQ0}),-1.0]])]});}
            var Q34;
            {var subQ0=sQuery(id+"F0.wireOp",EDGE,"E110.0.2.6");Q34=makeQuery(id+"F0.imprint","IMPRINT",FACE,{"disambiguationData":[TD([[makeQuery(id+"F0.imprint","IMPRINT",EDGE,{"derivedFrom":subQ0}),-1.0]])]});}
            var Q35;
            {var subQ0=sQuery(id+"F0.wireOp",EDGE,"E110.0.2.8");Q35=makeQuery(id+"F0.imprint","IMPRINT",FACE,{"disambiguationData":[TD([[makeQuery(id+"F0.imprint","IMPRINT",EDGE,{"derivedFrom":subQ0}),-1.0]])]});}
            var Q36;
            {var subQ0=sQuery(id+"F0.wireOp",EDGE,"E110.0.2.10");Q36=makeQuery(id+"F0.imprint","IMPRINT",FACE,{"disambiguationData":[TD([[makeQuery(id+"F0.imprint","IMPRINT",EDGE,{"derivedFrom":subQ0}),-1.0]])]});}
            var Q37;
            {var subQ0=sQuery(id+"F0.wireOp",EDGE,"E110.0.1.0");Q37=makeQuery(id+"F0.imprint","IMPRINT",FACE,{"disambiguationData":[TD([[makeQuery(id+"F0.imprint","IMPRINT",EDGE,{"derivedFrom":subQ0}),-1.0]])]});}
            var Q38;
            {var subQ0=sQuery(id+"F0.wireOp",EDGE,"E110.0.1.2");Q38=makeQuery(id+"F0.imprint","IMPRINT",FACE,{"disambiguationData":[TD([[makeQuery(id+"F0.imprint","IMPRINT",EDGE,{"derivedFrom":subQ0}),-1.0]])]});}
            var Q39;
            {var subQ0=sQuery(id+"F0.wireOp",EDGE,"E110.0.1.4");Q39=makeQuery(id+"F0.imprint","IMPRINT",FACE,{"disambiguationData":[TD([[makeQuery(id+"F0.imprint","IMPRINT",EDGE,{"derivedFrom":subQ0}),-1.0]])]});}
            var Q40;
            {var subQ0=sQuery(id+"F0.wireOp",EDGE,"E110.0.1.6");Q40=makeQuery(id+"F0.imprint","IMPRINT",FACE,{"disambiguationData":[TD([[makeQuery(id+"F0.imprint","IMPRINT",EDGE,{"derivedFrom":subQ0}),-1.0]])]});}
            var Q41;
            {var subQ0=sQuery(id+"F0.wireOp",EDGE,"E110.0.1.8");Q41=makeQuery(id+"F0.imprint","IMPRINT",FACE,{"disambiguationData":[TD([[makeQuery(id+"F0.imprint","IMPRINT",EDGE,{"derivedFrom":subQ0}),-1.0]])]});}
            var Q42;
            {var subQ0=sQuery(id+"F0.wireOp",EDGE,"E110.0.1.10");Q42=makeQuery(id+"F0.imprint","IMPRINT",FACE,{"disambiguationData":[TD([[makeQuery(id+"F0.imprint","IMPRINT",EDGE,{"derivedFrom":subQ0}),-1.0]])]});}
            var Q43;
            {var subQ0=sQuery(id+"F0.wireOp",EDGE,"E98");Q43=makeQuery(id+"F0.imprint","IMPRINT",FACE,{"disambiguationData":[TD([[makeQuery(id+"F0.imprint","IMPRINT",EDGE,{"derivedFrom":subQ0}),-1.0]])]});}
            var Q44;
            {var subQ0=sQuery(id+"F0.wireOp",EDGE,"E99");Q44=makeQuery(id+"F0.imprint","IMPRINT",FACE,{"disambiguationData":[TD([[makeQuery(id+"F0.imprint","IMPRINT",EDGE,{"derivedFrom":subQ0}),-1.0]])]});}
            var Q45;
            {var subQ0=sQuery(id+"F0.wireOp",EDGE,"E100");Q45=makeQuery(id+"F0.imprint","IMPRINT",FACE,{"disambiguationData":[TD([[makeQuery(id+"F0.imprint","IMPRINT",EDGE,{"derivedFrom":subQ0}),-1.0]])]});}
            var Q46;
            {var subQ0=sQuery(id+"F0.wireOp",EDGE,"E101");Q46=makeQuery(id+"F0.imprint","IMPRINT",FACE,{"disambiguationData":[TD([[makeQuery(id+"F0.imprint","IMPRINT",EDGE,{"derivedFrom":subQ0}),-1.0]])]});}
            var Q47;
            {var subQ0=sQuery(id+"F0.wireOp",EDGE,"E102");Q47=makeQuery(id+"F0.imprint","IMPRINT",FACE,{"disambiguationData":[TD([[makeQuery(id+"F0.imprint","IMPRINT",EDGE,{"derivedFrom":subQ0}),-1.0]])]});}
            var Q48;
            {var subQ0=sQuery(id+"F0.wireOp",EDGE,"E103");Q48=makeQuery(id+"F0.imprint","IMPRINT",FACE,{"disambiguationData":[TD([[makeQuery(id+"F0.imprint","IMPRINT",EDGE,{"derivedFrom":subQ0}),-1.0]])]});}
            extrude(context, id + "F1", {"entities" : qUnion([Q0, Q1, Q2, Q3, Q4, Q5, Q6, Q7, Q8, Q9, Q10, Q11, Q12, Q13, Q14, Q15, Q16, Q17, Q18, Q19, Q20, Q21, Q22, Q23, Q24, Q25, Q26, Q27, Q28, Q29, Q30, Q31, Q32, Q33, Q34, Q35, Q36, Q37, Q38, Q39, Q40, Q41, Q42, Q43, Q44, Q45, Q46, Q47, Q48]), "depth" : 3 * mm});
        }
    });
